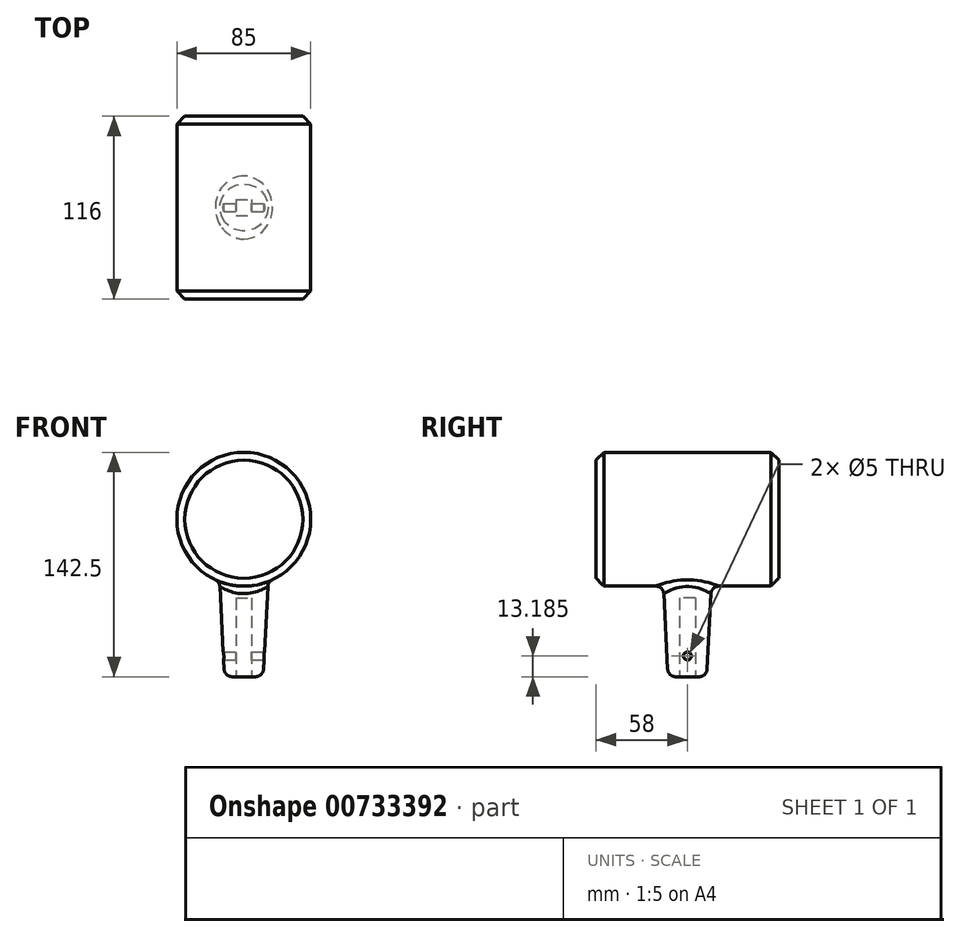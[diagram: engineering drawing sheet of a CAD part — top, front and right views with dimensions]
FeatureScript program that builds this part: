
annotation { "Feature Type Name" : "Feature", "Feature Type Description" : "" }
export const myFeature = defineFeature(function(context is Context, id is Id, definition is map)
    precondition{}
    {
        {
            var Q0;
            Q0=qCreatedBy(makeId("Front.planeOp"),FACE);
            var sketch = newSketch(context, id + "F0", { "sketchPlane" : qUnion([Q0])});
            skCircle(sketch, "E0", {"center": v(0, 0) * mm, "radius": 42.5 * mm});
            skSolve(sketch);
        }
        {
            var Q0;
            Q0 = qSketchRegion(id + "F0", true);
            extrude(context, id + "F1", {"entities" : qUnion([Q0]), "endBound" : BoundingType.SYMMETRIC, "depth" : 116 * mm, "offsetDistance" : 25 * mm});
        }
        {
            var Q0;
            Q0=qCreatedBy(makeId("Top.planeOp"),FACE);
            var sketch = newSketch(context, id + "F2", { "sketchPlane" : qUnion([Q0])});
            skCircle(sketch, "E1", {"center": v(0, 0) * mm, "radius": 17.5 * mm});
            skSolve(sketch);
        }
        {
            var Q0;
            Q0 = qSketchRegion(id + "F2", true);
            extrude(context, id + "F3", {"entities" : qUnion([Q0]), "operationType" : NewBodyOperationType.ADD, "oppositeDirection" : true, "depth" : 100 * mm, "offsetDistance" : 25 * mm, "hasDraft" : true, "draftAngle" : 3 * degree, "draftPullDirection" : true});
        }
        {
            var Q0;
            Q0=makeQuery(id+"F3.opExtrude","CAP_FACE",FACE,{"disambiguationData":[OSD([sQuery(id+"F2.wireOp",EDGE,"E1")])],"isStart":false});
            var sketch = newSketch(context, id + "F4", { "sketchPlane" : qUnion([Q0])});
            skLineSegment(sketch, "E2.bottom", {"start": v(-5, -5) * mm, "end": v(5, -5) * mm});
            skLineSegment(sketch, "E2.top", {"start": v(-5, 5) * mm, "end": v(5, 5) * mm});
            skLineSegment(sketch, "E2.left", {"start": v(-5, -5) * mm, "end": v(-5, 5) * mm});
            skLineSegment(sketch, "E2.right", {"start": v(5, -5) * mm, "end": v(5, 5) * mm});
            skPoint(sketch, "E2.middle", {"position": v(0, 0) * mm});
            skSolve(sketch);
        }
        {
            var Q0;
            Q0 = qSketchRegion(id + "F4", true);
            extrude(context, id + "F5", {"entities" : qUnion([Q0]), "operationType" : NewBodyOperationType.REMOVE, "oppositeDirection" : true, "depth" : 50 * mm, "offsetDistance" : 25 * mm});
        }
        {
            var Q0;
            Q0=qCreatedBy(makeId("Right.planeOp"),FACE);
            var sketch = newSketch(context, id + "F6", { "sketchPlane" : qUnion([Q0])});
            skCircle(sketch, "E3", {"center": v(0, -86.81) * mm, "radius": 2.5 * mm});
            skSolve(sketch);
        }
        {
            var Q0;
            Q0 = qSketchRegion(id + "F6", true);
            extrude(context, id + "F7", {"entities" : qUnion([Q0]), "operationType" : NewBodyOperationType.REMOVE, "endBound" : BoundingType.SYMMETRIC, "oppositeDirection" : true, "depth" : 100 * mm, "offsetDistance" : 25 * mm});
        }
        {
            var Q0;
            Q0=makeQuery(id+"F1.opExtrude","CAP_EDGE",EDGE,{"disambiguationData":[OSD([sQuery(id+"F0.wireOp",EDGE,"E0")])],"isStart":false});
            var Q1;
            Q1=makeQuery(id+"F1.opExtrude","CAP_EDGE",EDGE,{"disambiguationData":[OSD([sQuery(id+"F0.wireOp",EDGE,"E0")])],"isStart":true});
            chamfer(context, id + "F8", {"entities" : qUnion([Q0, Q1]), "width" : 5 * mm, "tangentPropagation" : true});
        }
        {
            var Q0;
            Q0=makeQuery(id+"F3.boolean.opBoolean","INTERSECT",EDGE,{"derivedFrom":[makeQuery(id+"F1.opExtrude","SWEPT_FACE",FACE,{"disambiguationData":[OSD([sQuery(id+"F0.wireOp",EDGE,"E0")])]}),makeQuery(id+"F3.opExtrude","SWEPT_FACE",FACE,{"disambiguationData":[OSD([sQuery(id+"F2.wireOp",EDGE,"E1")])]})]});
            fillet(context, id + "F9", {"entities" : qUnion([Q0]), "radius" : 5 * mm, "tangentPropagation" : true, "allowEdgeOverflow" : false});
        }
        {
            var Q0;
            Q0=makeQuery(id+"F3.opExtrude","CAP_EDGE",EDGE,{"disambiguationData":[OSD([sQuery(id+"F2.wireOp",EDGE,"E1")])],"isStart":false});
            fillet(context, id + "F10", {"entities" : qUnion([Q0]), "radius" : 5 * mm, "tangentPropagation" : true, "allowEdgeOverflow" : false});
        }
    });
